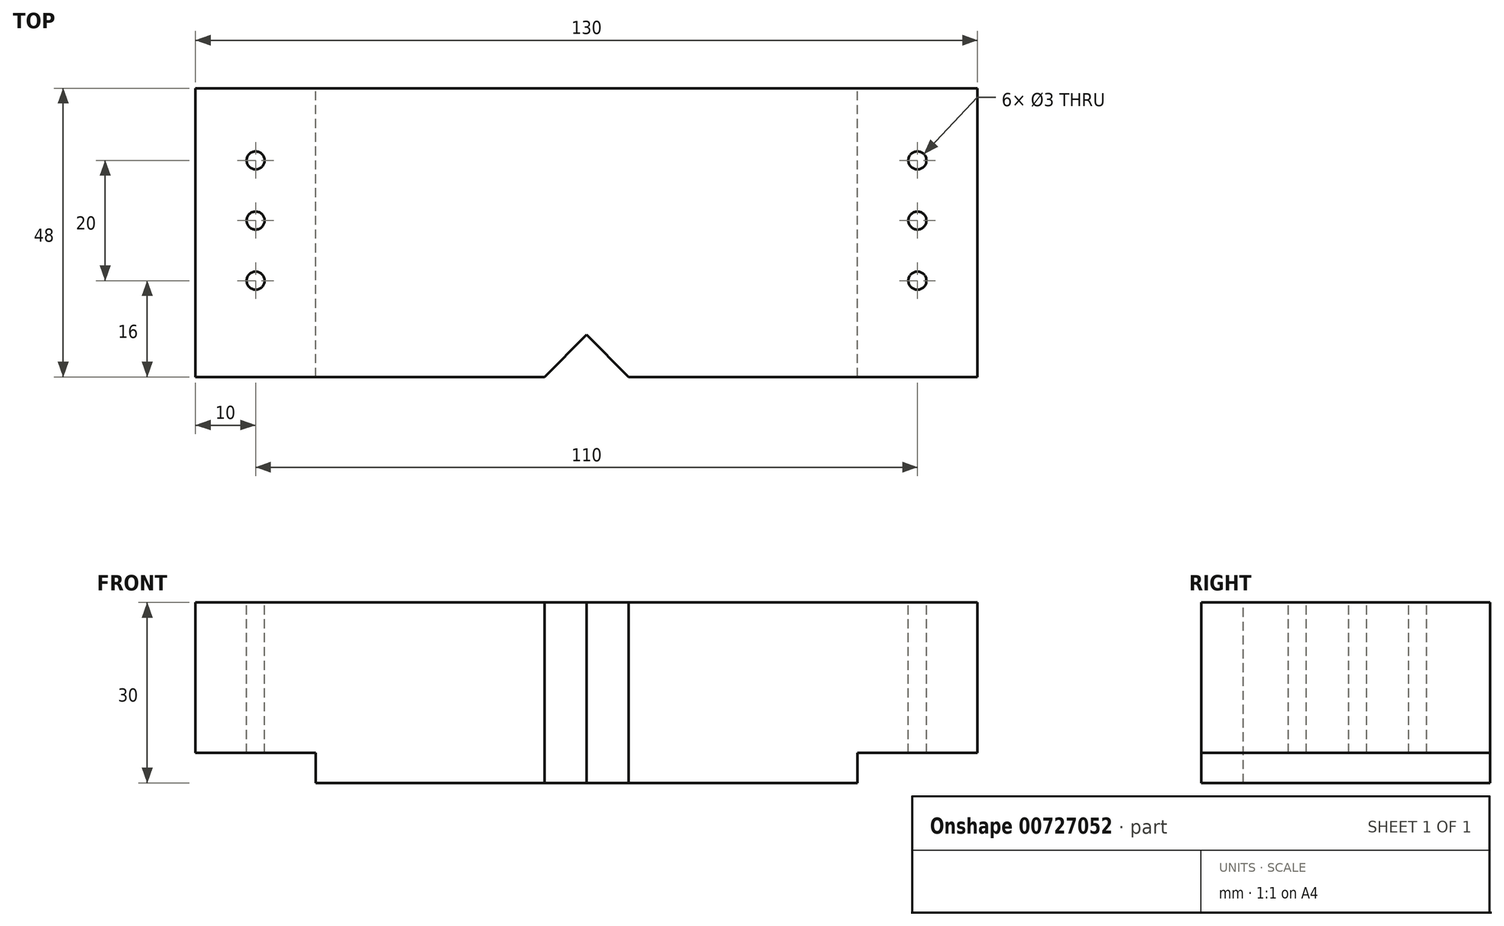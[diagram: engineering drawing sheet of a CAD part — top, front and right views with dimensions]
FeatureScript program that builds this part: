
annotation { "Feature Type Name" : "Feature", "Feature Type Description" : "" }
export const myFeature = defineFeature(function(context is Context, id is Id, definition is map)
    precondition{}
    {
        {
            var Q0;
            Q0=qCreatedBy(makeId("Top.planeOp"),FACE);
            var sketch = newSketch(context, id + "F0", { "sketchPlane" : qUnion([Q0])});
            skLineSegment(sketch, "E0.bottom", {"start": v(65, 24) * mm, "end": v(-65, 24) * mm});
            skLineSegment(sketch, "E0.top", {"start": v(65, -24) * mm, "end": v(-65, -24) * mm});
            skLineSegment(sketch, "E0.left", {"start": v(65, 24) * mm, "end": v(65, -24) * mm});
            skLineSegment(sketch, "E0.right", {"start": v(-65, 24) * mm, "end": v(-65, -24) * mm});
            skPoint(sketch, "E0.middle", {"position": v(0, 0) * mm});
            skSolve(sketch);
        }
        {
            var Q0;
            Q0 = qSketchRegion(id + "F0", true);
            extrude(context, id + "F1", {"entities" : qUnion([Q0]), "depth" : 25 * mm, "offsetDistance" : 25 * mm});
        }
        {
            var Q0;
            Q0=makeQuery(id+"F1.opExtrude","CAP_FACE",FACE,{"disambiguationData":[OSD([sQuery(id+"F0.wireOp",EDGE,"E0.bottom"),sQuery(id+"F0.wireOp",EDGE,"E0.top"),sQuery(id+"F0.wireOp",EDGE,"E0.left"),sQuery(id+"F0.wireOp",EDGE,"E0.right")])],"isStart":false});
            var sketch = newSketch(context, id + "F2", { "sketchPlane" : qUnion([Q0])});
            skLineSegment(sketch, "E1", {"start": v(0, -17) * mm, "end": v(-7, -24) * mm});
            skLineSegment(sketch, "E2", {"start": v(0, -17) * mm, "end": v(7, -24) * mm});
            skLineSegment(sketch, "E3", {"start": v(-7, -24) * mm, "end": v(7, -24) * mm});
            skSolve(sketch);
        }
        {
            var Q0;
            Q0 = qSketchRegion(id + "F2", true);
            extrude(context, id + "F3", {"entities" : qUnion([Q0]), "operationType" : NewBodyOperationType.REMOVE, "endBound" : BoundingType.THROUGH_ALL, "oppositeDirection" : true, "depth" : 25 * mm, "offsetDistance" : 25 * mm});
        }
        {
            var Q0;
            Q0=makeQuery(id+"F1.opExtrude","CAP_FACE",FACE,{"disambiguationData":[OSD([sQuery(id+"F0.wireOp",EDGE,"E0.bottom"),sQuery(id+"F0.wireOp",EDGE,"E0.top"),sQuery(id+"F0.wireOp",EDGE,"E0.left"),sQuery(id+"F0.wireOp",EDGE,"E0.right")])],"isStart":false});
            var sketch = newSketch(context, id + "F4", { "sketchPlane" : qUnion([Q0])});
            skCircle(sketch, "E4", {"center": v(-55, 12) * mm, "radius": 1.5 * mm});
            skCircle(sketch, "E5", {"center": v(-55, 2) * mm, "radius": 1.5 * mm});
            skCircle(sketch, "E6", {"center": v(-55, -8) * mm, "radius": 1.5 * mm});
            skCircle(sketch, "E7.MirrorC", {"center": v(55, 12) * mm, "radius": 1.5 * mm});
            skCircle(sketch, "E8.MirrorC", {"center": v(55, 2) * mm, "radius": 1.5 * mm});
            skCircle(sketch, "E9.MirrorC", {"center": v(55, -8) * mm, "radius": 1.5 * mm});
            skSolve(sketch);
        }
        {
            var Q0;
            Q0 = qSketchRegion(id + "F4", true);
            extrude(context, id + "F5", {"entities" : qUnion([Q0]), "operationType" : NewBodyOperationType.REMOVE, "endBound" : BoundingType.THROUGH_ALL, "oppositeDirection" : true, "depth" : 25 * mm, "offsetDistance" : 25 * mm});
        }
        {
            var Q0;
            Q0=makeQuery(id+"F1.opExtrude","CAP_FACE",FACE,{"disambiguationData":[OSD([sQuery(id+"F0.wireOp",EDGE,"E0.bottom"),sQuery(id+"F0.wireOp",EDGE,"E0.top"),sQuery(id+"F0.wireOp",EDGE,"E0.left"),sQuery(id+"F0.wireOp",EDGE,"E0.right")])],"isStart":true});
            var sketch = newSketch(context, id + "F6", { "sketchPlane" : qUnion([Q0])});
            skLineSegment(sketch, "E10.bottom", {"start": v(-45, 24) * mm, "end": v(45, 24) * mm});
            skLineSegment(sketch, "E10.top", {"start": v(-45, -24) * mm, "end": v(45, -24) * mm});
            skLineSegment(sketch, "E10.left", {"start": v(-45, 24) * mm, "end": v(-45, -24) * mm});
            skLineSegment(sketch, "E10.right", {"start": v(45, 24) * mm, "end": v(45, -24) * mm});
            skSolve(sketch);
        }
        {
            var Q0;
            Q0 = qSketchRegion(id + "F6", true);
            extrude(context, id + "F7", {"entities" : qUnion([Q0]), "operationType" : NewBodyOperationType.ADD, "depth" : 5 * mm, "offsetDistance" : 25 * mm});
        }
        {
            var Q0;
            Q0=makeQuery(id+"F7.opExtrude","CAP_FACE",FACE,{"disambiguationData":[OSD([sQuery(id+"F6.wireOp",EDGE,"E10.bottom"),sQuery(id+"F6.wireOp",EDGE,"E10.top"),sQuery(id+"F6.wireOp",EDGE,"E10.left"),sQuery(id+"F6.wireOp",EDGE,"E10.right")])],"isStart":true});
            extrude(context, id + "F8", {"entities" : qUnion([Q0]), "operationType" : NewBodyOperationType.REMOVE, "oppositeDirection" : true, "depth" : 25 * mm, "offsetDistance" : 25 * mm});
        }
    });
